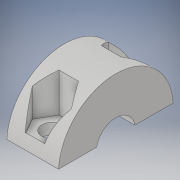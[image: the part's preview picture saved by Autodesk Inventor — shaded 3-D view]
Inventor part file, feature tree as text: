
AUTODESK INVENTOR PART (.ipt)
format: ipt  version: 2019 (Build 230136000, 136)  size: 173,056 bytes
history: native  units: mm
features: sketch x5, extrude x4, plane x2, hole x1, mirror x1
ambient origin geometry x8: Origin, YZ Plane, XZ Plane, XY Plane, X Axis, Y Axis, Z Axis, Center Point
bodies: Solid1 (feature_tree)
feature tree (13):
  extrude  "Extrusion1"  Depth=20.0mm
  extrude  "Extrusion3"  Depth=3.490659mm
  plane  "Work Plane1"
  extrude  "Extrusion4"  Depth=9.0mm
  plane  "Work Plane2"
  hole  "Hole1"  [1 undecoded]
  mirror  "Mirror1"
  extrude  "Extrusion6"  Depth=7.5mm TaperAngle=0.0deg
  sketch  "Sketch1"  dims[d0=6.75mm d1=20.0mm]
  sketch  "Sketch3"  dims[d2=13.962634mm d3=3.490659mm]
  sketch  "Sketch4"  dims[d4=9.0mm d5=0.0mm d9=15.0mm]
  sketch  "Sketch5"  dims[d10=0.5mm d11=0.0mm d12=10.0mm]
  sketch  "Sketch8"  dims[d13=5.9mm d14=7.5mm d15=0.0mm d16=-20.0mm d17=3.5mm d18=6.0mm d19=6.0mm d20=7.5mm d21=90.0deg d22=8.0mm d23=0.0mm d29=10.0mm d30=0.0mm]
note: 1 required parameter value undecoded (feature->parameter linkage not recoverable at this tier; creation-order binding heuristic only, values carry confidence <= 0.55)
